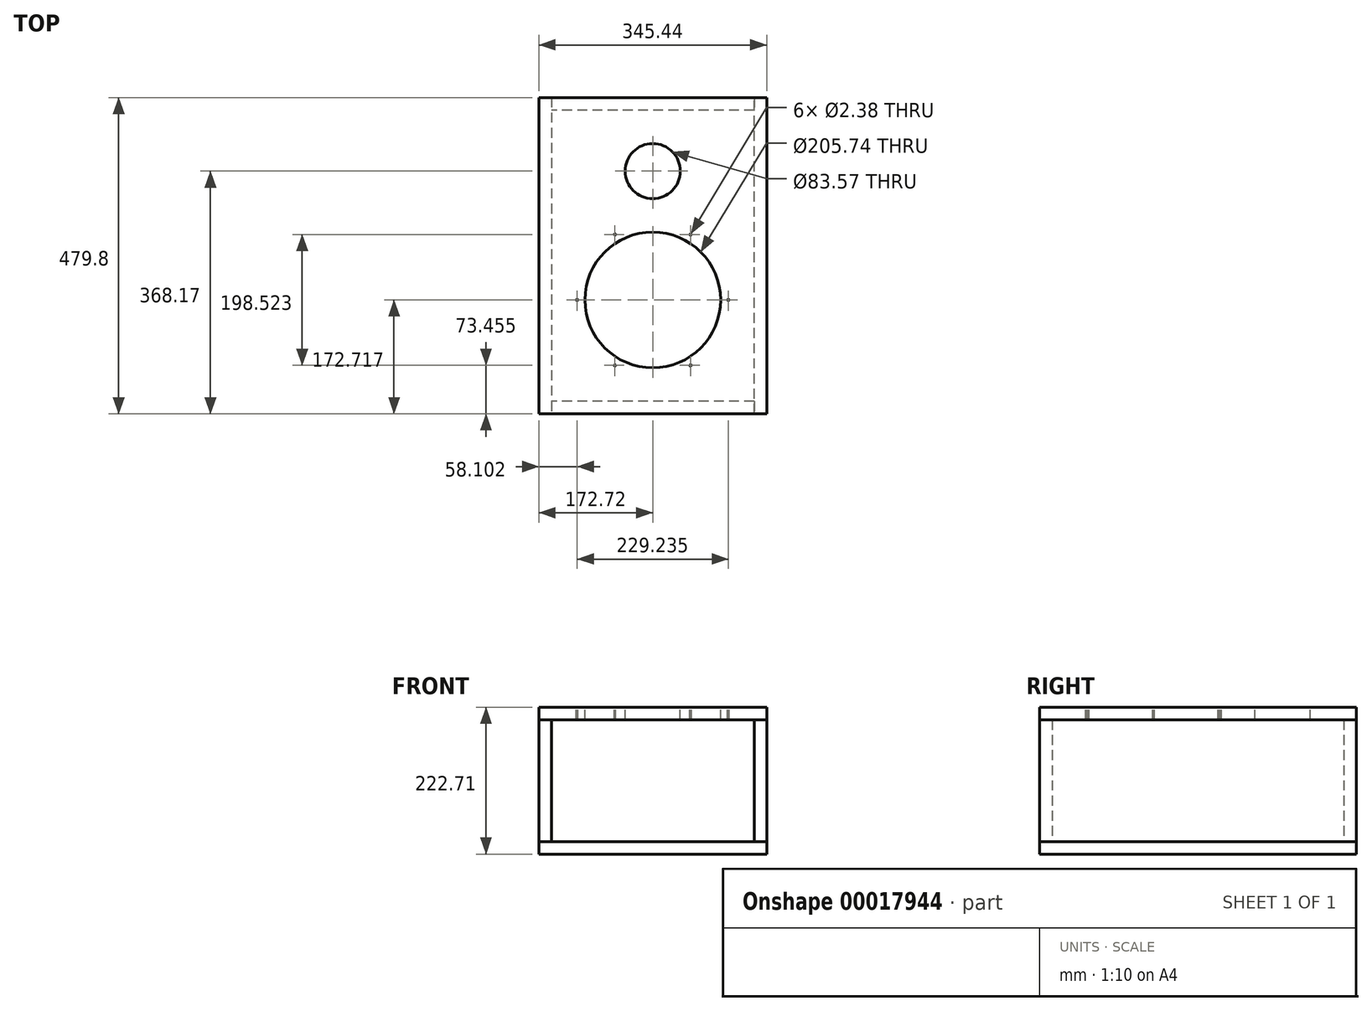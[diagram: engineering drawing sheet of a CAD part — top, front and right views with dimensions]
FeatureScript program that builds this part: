
annotation { "Feature Type Name" : "Feature", "Feature Type Description" : "" }
export const myFeature = defineFeature(function(context is Context, id is Id, definition is map)
    precondition{}
    {
        {
            var Q0;
            Q0=qCreatedBy(makeId("Top.planeOp"),FACE);
            var sketch = newSketch(context, id + "F0", { "sketchPlane" : qUnion([Q0])});
            skLineSegment(sketch, "E0.bottom", {"start": v(172.72, -239.9) * mm, "end": v(-172.72, -239.9) * mm});
            skLineSegment(sketch, "E0.top", {"start": v(172.72, 239.9) * mm, "end": v(-172.72, 239.9) * mm});
            skLineSegment(sketch, "E0.left", {"start": v(172.72, -239.9) * mm, "end": v(172.72, 239.9) * mm});
            skLineSegment(sketch, "E0.right", {"start": v(-172.72, -239.9) * mm, "end": v(-172.72, 239.9) * mm});
            skPoint(sketch, "E0.middle", {"position": v(0, 0) * mm});
            skSolve(sketch);
        }
        {
            var Q0;
            Q0 = qSketchRegion(id + "F0", true);
            extrude(context, id + "F1", {"entities" : qUnion([Q0]), "depth" : 19.05 * mm, "offsetDistance" : 25.4 * mm});
        }
        {
            var Q0;
            Q0=makeQuery(id+"F1.opExtrude","CAP_FACE",FACE,{"disambiguationData":[OSD([sQuery(id+"F0.wireOp",EDGE,"E0.bottom"),sQuery(id+"F0.wireOp",EDGE,"E0.top"),sQuery(id+"F0.wireOp",EDGE,"E0.left"),sQuery(id+"F0.wireOp",EDGE,"E0.right")])],"isStart":false});
            var sketch = newSketch(context, id + "F2", { "sketchPlane" : qUnion([Q0])});
            skLineSegment(sketch, "E1.bottom", {"start": v(-172.72, 239.9) * mm, "end": v(-153.67, 239.9) * mm});
            skLineSegment(sketch, "E1.top", {"start": v(-172.72, -239.9) * mm, "end": v(-153.67, -239.9) * mm});
            skLineSegment(sketch, "E1.left", {"start": v(-172.72, 239.9) * mm, "end": v(-172.72, -239.9) * mm});
            skLineSegment(sketch, "E1.right", {"start": v(-153.67, 239.9) * mm, "end": v(-153.67, -239.9) * mm});
            skSolve(sketch);
        }
        {
            var Q0;
            Q0 = qSketchRegion(id + "F2", true);
            extrude(context, id + "F3", {"entities" : qUnion([Q0]), "depth" : 184.6 * mm, "offsetDistance" : 25.4 * mm});
        }
        {
            var Q0;
            Q0=makeQuery(id+"F3.opExtrude","SWEPT_BODY",BODY,{"disambiguationData":[OSD([sQuery(id+"F2.wireOp",EDGE,"E1.bottom"),sQuery(id+"F2.wireOp",EDGE,"E1.top"),sQuery(id+"F2.wireOp",EDGE,"E1.left"),sQuery(id+"F2.wireOp",EDGE,"E1.right")])]});
            transform(context, id + "F4", {"entities" : qUnion([Q0]), "transformType" : TransformType.TRANSLATION_3D, "dx" : 326.4 * mm, "dy" : 0 * mm, "dz" : 0 * mm, "makeCopy" : true});
        }
        {
            var Q0;
            Q0=makeQuery(id+"F1.opExtrude","CAP_FACE",FACE,{"disambiguationData":[OSD([sQuery(id+"F0.wireOp",EDGE,"E0.bottom"),sQuery(id+"F0.wireOp",EDGE,"E0.top"),sQuery(id+"F0.wireOp",EDGE,"E0.left"),sQuery(id+"F0.wireOp",EDGE,"E0.right")])],"isStart":false});
            var sketch = newSketch(context, id + "F5", { "sketchPlane" : qUnion([Q0])});
            skLineSegment(sketch, "E2.bottom", {"start": v(153.67, 239.9) * mm, "end": v(-153.67, 239.9) * mm});
            skLineSegment(sketch, "E2.top", {"start": v(153.67, 220.85) * mm, "end": v(-153.67, 220.85) * mm});
            skLineSegment(sketch, "E2.left", {"start": v(153.67, 239.9) * mm, "end": v(153.67, 220.85) * mm});
            skLineSegment(sketch, "E2.right", {"start": v(-153.67, 239.9) * mm, "end": v(-153.67, 220.85) * mm});
            skSolve(sketch);
        }
        {
            var Q0;
            Q0 = qSketchRegion(id + "F5", true);
            extrude(context, id + "F6", {"entities" : qUnion([Q0]), "depth" : 184.6 * mm, "offsetDistance" : 25.4 * mm});
        }
        {
            var Q0;
            Q0=makeQuery(id+"F6.opExtrude","SWEPT_BODY",BODY,{"disambiguationData":[OSD([sQuery(id+"F5.wireOp",EDGE,"E2.bottom"),sQuery(id+"F5.wireOp",EDGE,"E2.top"),sQuery(id+"F5.wireOp",EDGE,"E2.left"),sQuery(id+"F5.wireOp",EDGE,"E2.right")])]});
            transform(context, id + "F7", {"entities" : qUnion([Q0]), "transformType" : TransformType.TRANSLATION_3D, "dx" : 0 * mm, "dy" : -460.76 * mm, "dz" : 0 * mm, "makeCopy" : true});
        }
        {
            var Q0;
            Q0=makeQuery(id+"F1.opExtrude","SWEPT_BODY",BODY,{"disambiguationData":[OSD([sQuery(id+"F0.wireOp",EDGE,"E0.bottom"),sQuery(id+"F0.wireOp",EDGE,"E0.top"),sQuery(id+"F0.wireOp",EDGE,"E0.left"),sQuery(id+"F0.wireOp",EDGE,"E0.right")])]});
            transform(context, id + "F8", {"entities" : qUnion([Q0]), "transformType" : TransformType.TRANSLATION_3D, "dx" : 0 * mm, "dy" : 0 * mm, "dz" : 203.66 * mm, "makeCopy" : true});
        }
        {
            var Q0;
            Q0=makeQuery(id+"F8.opPattern","COPY",FACE,{"derivedFrom":makeQuery(id+"F1.opExtrude","CAP_FACE",FACE,{"disambiguationData":[OSD([sQuery(id+"F0.wireOp",EDGE,"E0.bottom"),sQuery(id+"F0.wireOp",EDGE,"E0.top"),sQuery(id+"F0.wireOp",EDGE,"E0.left"),sQuery(id+"F0.wireOp",EDGE,"E0.right")])],"isStart":false}),"instanceName":"1"});
            var sketch = newSketch(context, id + "F9", { "sketchPlane" : qUnion([Q0])});
            skCircle(sketch, "E3", {"center": v(0, -67.18) * mm, "radius": 102.87 * mm});
            skCircle(sketch, "E4", {"center": v(0, 128.27) * mm, "radius": 41.78 * mm});
            skCircle(sketch, "E5", {"center": v(114.62, -67.18) * mm, "radius": 1.2 * mm});
            skCircle(sketch, "E6.1.0", {"center": v(57.3, 32.08) * mm, "radius": 1.2 * mm});
            skCircle(sketch, "E6.2.0", {"center": v(-57.3, 32.08) * mm, "radius": 1.2 * mm});
            skCircle(sketch, "E6.3.0", {"center": v(-114.62, -67.18) * mm, "radius": 1.2 * mm});
            skCircle(sketch, "E6.4.0", {"center": v(-57.3, -166.44) * mm, "radius": 1.2 * mm});
            skCircle(sketch, "E6.5.0", {"center": v(57.3, -166.44) * mm, "radius": 1.2 * mm});
            skSolve(sketch);
        }
        {
            var Q0;
            Q0 = qSketchRegion(id + "F9", true);
            extrude(context, id + "F10", {"entities" : qUnion([Q0]), "operationType" : NewBodyOperationType.REMOVE, "oppositeDirection" : true, "depth" : 25.4 * mm, "offsetDistance" : 25.4 * mm});
        }
    });
